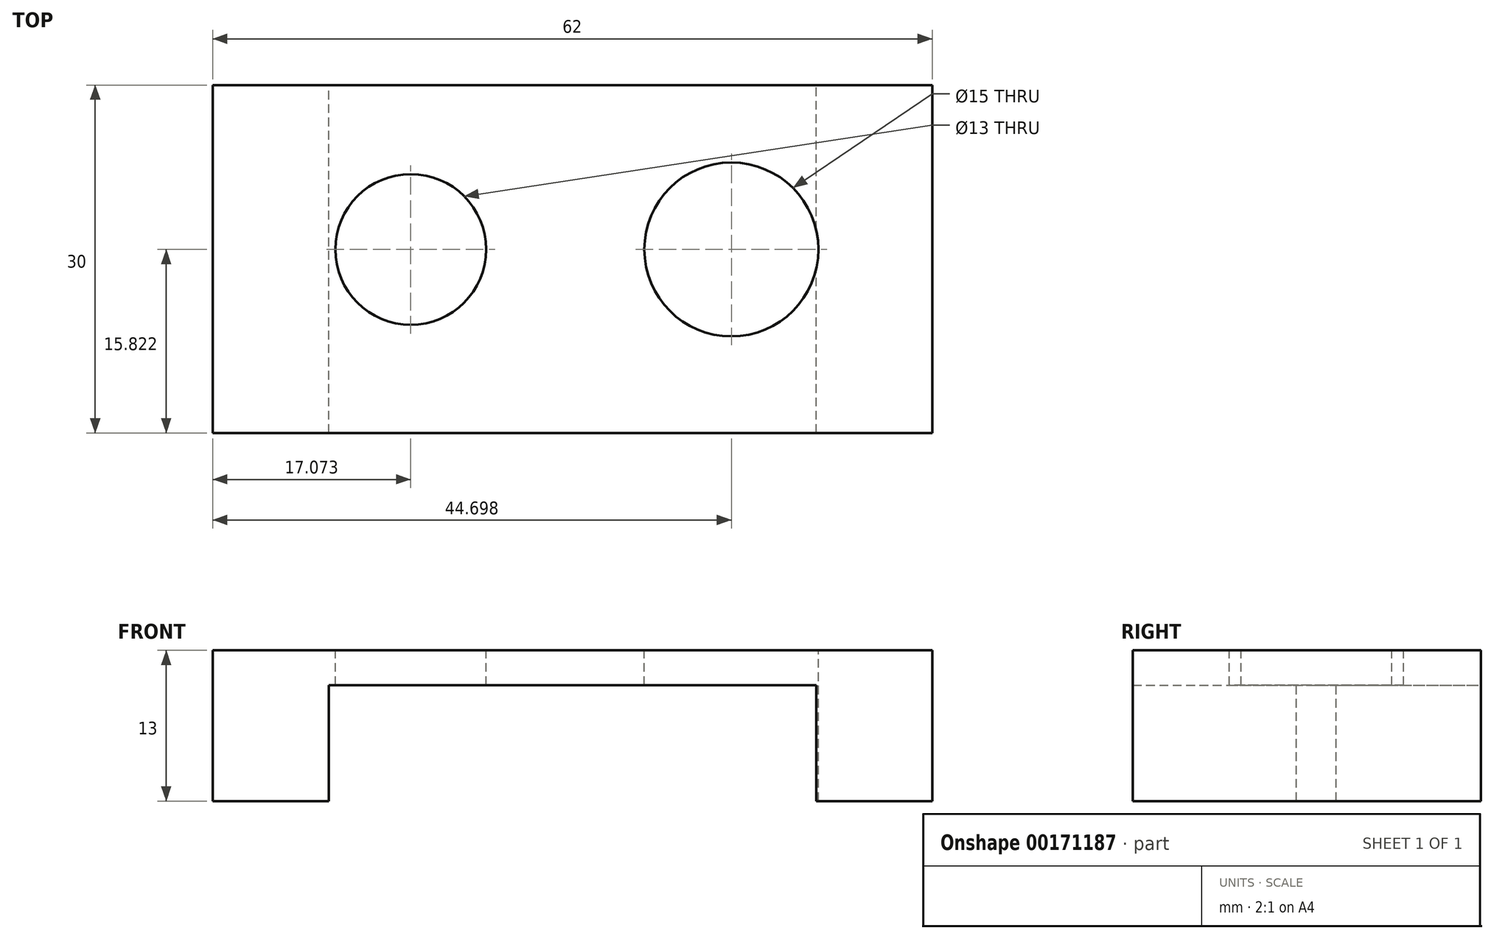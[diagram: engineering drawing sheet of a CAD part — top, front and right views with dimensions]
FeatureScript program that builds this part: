
annotation { "Feature Type Name" : "Feature", "Feature Type Description" : "" }
export const myFeature = defineFeature(function(context is Context, id is Id, definition is map)
    precondition{}
    {
        {
            var Q0;
            Q0=qCreatedBy(makeId("Front.planeOp"),FACE);
            var sketch = newSketch(context, id + "F0", { "sketchPlane" : qUnion([Q0])});
            skLineSegment(sketch, "E0", {"start": v(0, 0) * mm, "end": v(0, -13) * mm});
            skLineSegment(sketch, "E1", {"start": v(0, -13) * mm, "end": v(10, -13) * mm});
            skLineSegment(sketch, "E2", {"start": v(10, -13) * mm, "end": v(10, -3) * mm});
            skLineSegment(sketch, "E3", {"start": v(10, -3) * mm, "end": v(52, -3) * mm});
            skLineSegment(sketch, "E4", {"start": v(52, -3) * mm, "end": v(52, -13) * mm});
            skLineSegment(sketch, "E5", {"start": v(52, -13) * mm, "end": v(62, -13) * mm});
            skLineSegment(sketch, "E6", {"start": v(61.8, -13) * mm, "end": v(62, 0) * mm});
            skLineSegment(sketch, "E7", {"start": v(62, 0) * mm, "end": v(0, 0) * mm});
            skLineSegment(sketch, "E8", {"start": v(62, -13) * mm, "end": v(62, 0) * mm});
            skSolve(sketch);
        }
        {
            var Q0;
            Q0 = qSketchRegion(id + "F0", true);
            extrude(context, id + "F1", {"entities" : qUnion([Q0]), "depth" : 30 * mm});
        }
        {
            var Q0;
            Q0=makeQuery(id+"F1.opExtrude","SWEPT_FACE",FACE,{"disambiguationData":[OSD([sQuery(id+"F0.wireOp",EDGE,"E7")])]});
            var sketch = newSketch(context, id + "F2", { "sketchPlane" : qUnion([Q0])});
            skCircle(sketch, "E9", {"center": v(44.7, -14.18) * mm, "radius": 7.5 * mm});
            skCircle(sketch, "E10", {"center": v(17.07, -14.18) * mm, "radius": 6.5 * mm});
            skSolve(sketch);
        }
        {
            var Q0;
            Q0 = qSketchRegion(id + "F2", true);
            extrude(context, id + "F3", {"entities" : qUnion([Q0]), "operationType" : NewBodyOperationType.REMOVE, "endBound" : BoundingType.THROUGH_ALL, "oppositeDirection" : true, "depth" : 25 * mm});
        }
    });
